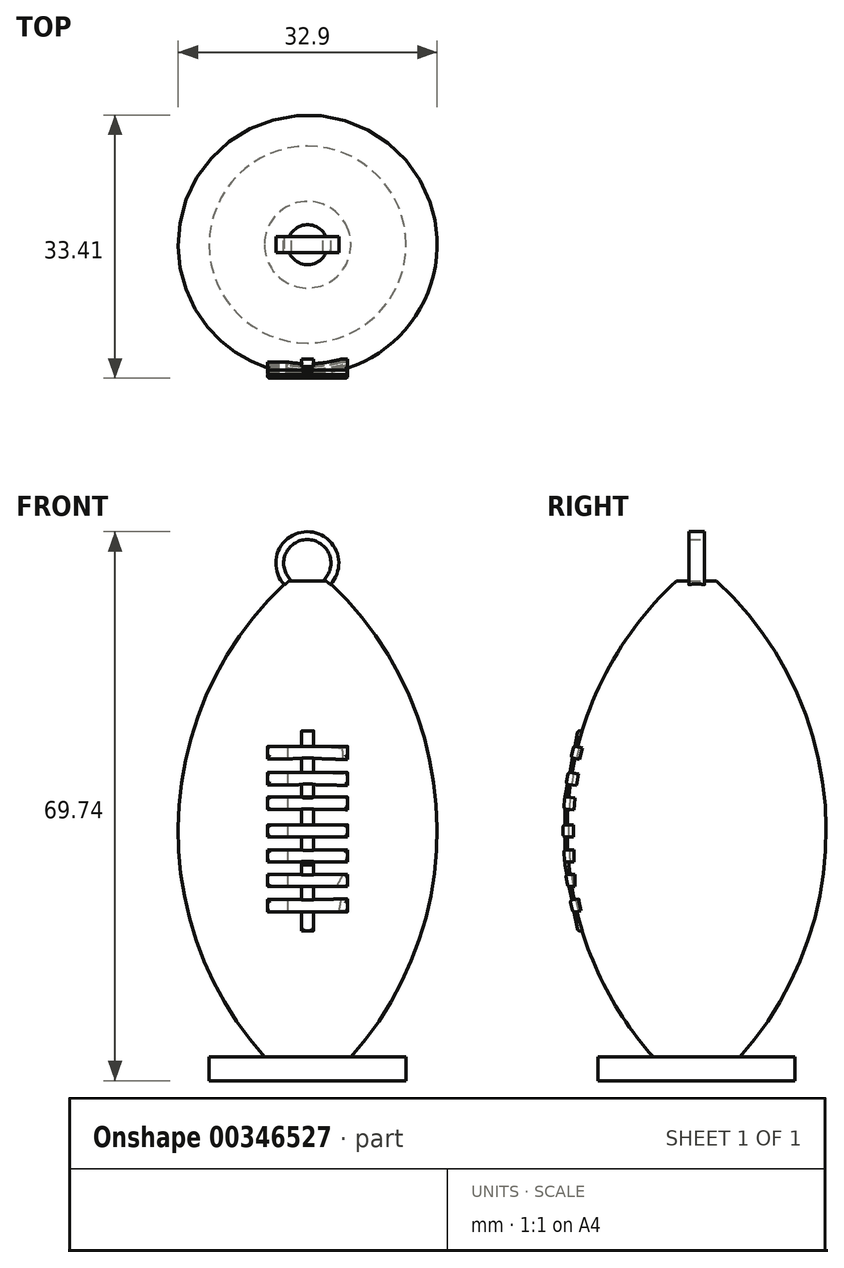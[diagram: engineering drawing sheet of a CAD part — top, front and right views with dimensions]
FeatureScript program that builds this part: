
annotation { "Feature Type Name" : "Feature", "Feature Type Description" : "" }
export const myFeature = defineFeature(function(context is Context, id is Id, definition is map)
    precondition{}
    {
        {
            var Q0;
            Q0=qCreatedBy(makeId("Front.planeOp"),FACE);
            var sketch = newSketch(context, id + "F0", { "sketchPlane" : qUnion([Q0])});
            skLineSegment(sketch, "E0", {"start": v(0, 0) * mm, "end": v(0, 63.5) * mm});
            skLineSegment(sketch, "E1", {"start": v(0, 0) * mm, "end": v(2.54, 0) * mm});
            skLineSegment(sketch, "E2", {"start": v(2.54, 0) * mm, "end": v(2.54, 63.5) * mm});
            skLineSegment(sketch, "E3", {"start": v(2.54, 63.5) * mm, "end": v(0, 63.5) * mm});
            skArc(sketch, "E4", {"start": v(0, 63.5) * mm, "mid": v(-13.91, 31.75) * mm, "end": v(0, 0) * mm});
            skSolve(sketch);
        }
        {
            var Q0;
            Q0=makeQuery(id+"F0.imprint","IMPRINT",FACE,{"disambiguationData":[TD([[makeQuery(id+"F0.imprint","IMPRINT",EDGE,{"derivedFrom":sQuery(id+"F0.wireOp",EDGE,"E0")}),1.0]])]});
            var Q1;
            Q1=sQuery(id+"F0.wireOp",EDGE,"E2");
            revolve(context, id + "F1", {"entities" : qUnion([Q0]), "axis" : qUnion([Q1]), "revolveType" : RevolveType.FULL});
        }
        {
            var Q0;
            Q0=qCreatedBy(makeId("Front.planeOp"),FACE);
            var sketch = newSketch(context, id + "F2", { "sketchPlane" : qUnion([Q0])});
            skLineSegment(sketch, "E5", {"start": v(0, 63.5) * mm, "end": v(2.54, 63.5) * mm});
            skLineSegment(sketch, "E6", {"start": v(0, 63.5) * mm, "end": v(2.03, 65.95) * mm});
            skLineSegment(sketch, "E7", {"start": v(2.03, 65.95) * mm, "end": v(2.54, 65.95) * mm});
            skLineSegment(sketch, "E8", {"start": v(2.54, 65.95) * mm, "end": v(2.54, 63.5) * mm});
            skLineSegment(sketch, "E9.left", {"start": v(0, 63.5) * mm, "end": v(0, 0) * mm});
            skLineSegment(sketch, "E9.right", {"start": v(2.54, 63.5) * mm, "end": v(2.54, 0) * mm});
            skLineSegment(sketch, "E10.bottom", {"start": v(0, 0) * mm, "end": v(2.54, 0) * mm});
            skLineSegment(sketch, "E10.top", {"start": v(0, -2.54) * mm, "end": v(2.54, -2.54) * mm});
            skLineSegment(sketch, "E10.left", {"start": v(0, 0) * mm, "end": v(0, -2.54) * mm});
            skLineSegment(sketch, "E10.right", {"start": v(2.54, 0) * mm, "end": v(2.54, -2.54) * mm});
            skSolve(sketch);
        }
        {
            var Q0;
            Q0=makeQuery(id+"F2.imprint","IMPRINT",FACE,{"disambiguationData":[TD([[makeQuery(id+"F2.imprint","IMPRINT",EDGE,{"derivedFrom":sQuery(id+"F2.wireOp",EDGE,"E5")}),-1.0]])]});
            var Q1;
            Q1=sQuery(id+"F2.wireOp",EDGE,"E9.right");
            revolve(context, id + "F3", {"operationType" : NewBodyOperationType.ADD, "entities" : qUnion([Q0]), "axis" : qUnion([Q1]), "revolveType" : RevolveType.FULL});
        }
        {
            var Q0;
            Q0=makeQuery(id+"F3.opRevolve","SWEPT_FACE",FACE,{"disambiguationData":[OSD([sQuery(id+"F2.wireOp",EDGE,"E10.bottom")])]});
            var sketch = newSketch(context, id + "F4", { "sketchPlane" : qUnion([Q0])});
            skLineSegment(sketch, "E11.bottom", {"start": v(4.34, -1.8) * mm, "end": v(0.74, -1.8) * mm});
            skLineSegment(sketch, "E11.top", {"start": v(4.34, 1.8) * mm, "end": v(0.74, 1.8) * mm});
            skLineSegment(sketch, "E11.left", {"start": v(4.34, -1.8) * mm, "end": v(4.34, 1.8) * mm});
            skLineSegment(sketch, "E11.right", {"start": v(0.74, -1.8) * mm, "end": v(0.74, 1.8) * mm});
            skPoint(sketch, "E11.middle", {"position": v(2.54, 0) * mm});
            skCircle(sketch, "E12", {"center": v(2.54, 0) * mm, "radius": 12.5 * mm});
            skSolve(sketch);
        }
        {
            var Q0;
            Q0=makeQuery(id+"F4.imprint","IMPRINT",FACE,{"disambiguationData":[TD([[makeQuery(id+"F4.imprint","IMPRINT",EDGE,{"derivedFrom":sQuery(id+"F4.wireOp",EDGE,"E11.bottom")}),-1.0]])]});
            var Q1;
            Q1=makeQuery(id+"F4.imprint","IMPRINT",FACE,{"disambiguationData":[TD([[makeQuery(id+"F4.imprint","IMPRINT",EDGE,{"derivedFrom":sQuery(id+"F4.wireOp",EDGE,"E12")}),1.0]])]});
            var Q2;
            {var subQ0=sQuery(id+"F4.wireOp",EDGE,"E11.bottom");Q2=makeQuery(id+"F4.imprint","IMPRINT",FACE,{"disambiguationData":[TD([[makeQuery(id+"F4.imprint","IMPRINT",EDGE,{"derivedFrom":subQ0}),1.0]])]});}
            var Q3;
            {var subQ0=sQuery(id+"F4.wireOp",EDGE,"E11.left");Q3=makeQuery(id+"F4.imprint","IMPRINT",FACE,{"disambiguationData":[TD([[makeQuery(id+"F4.imprint","IMPRINT",EDGE,{"derivedFrom":subQ0}),-1.0]])]});}
            var Q4;
            {var subQ0=sQuery(id+"F4.wireOp",EDGE,"E11.top");Q4=makeQuery(id+"F4.imprint","IMPRINT",FACE,{"disambiguationData":[TD([[makeQuery(id+"F4.imprint","IMPRINT",EDGE,{"derivedFrom":subQ0}),-1.0]])]});}
            var Q5;
            {var subQ0=sQuery(id+"F4.wireOp",EDGE,"E11.right");Q5=makeQuery(id+"F4.imprint","IMPRINT",FACE,{"disambiguationData":[TD([[makeQuery(id+"F4.imprint","IMPRINT",EDGE,{"derivedFrom":subQ0}),1.0]])]});}
            extrude(context, id + "F5", {"entities" : qUnion([Q0, Q1, Q2, Q3, Q4, Q5]), "operationType" : NewBodyOperationType.ADD, "oppositeDirection" : true, "depth" : 3 * mm, "offsetDistance" : 25 * mm});
        }
        {
            var Q0;
            Q0=qCreatedBy(makeId("Right.planeOp"),FACE);
            var sketch = newSketch(context, id + "F6", { "sketchPlane" : qUnion([Q0])});
            skLineSegment(sketch, "E13", {"start": v(0, 0) * mm, "end": v(0, 63.5) * mm});
            skLineSegment(sketch, "E14", {"start": v(0, 63.5) * mm, "end": v(-3.05, 63.5) * mm});
            skLineSegment(sketch, "E15", {"start": v(-3.05, 63.5) * mm, "end": v(-3.05, 0) * mm});
            skLineSegment(sketch, "E16", {"start": v(-3.05, 0) * mm, "end": v(0, 0) * mm});
            skArc(sketch, "E17", {"start": v(-3.05, 63.5) * mm, "mid": v(-16.96, 31.75) * mm, "end": v(-3.05, 0) * mm});
            skLineSegment(sketch, "E18.bottom", {"start": v(-16.96, 32.51) * mm, "end": v(-15.63, 32.51) * mm});
            skLineSegment(sketch, "E18.top", {"start": v(-16.96, 30.99) * mm, "end": v(-15.63, 30.99) * mm});
            skLineSegment(sketch, "E18.left", {"start": v(-16.96, 32.51) * mm, "end": v(-16.96, 30.99) * mm});
            skLineSegment(sketch, "E18.right", {"start": v(-15.63, 32.51) * mm, "end": v(-15.63, 30.99) * mm});
            skLineSegment(sketch, "E19", {"start": v(-15.2, 34.39) * mm, "end": v(-15.08, 35.9) * mm});
            skLineSegment(sketch, "E20", {"start": v(-15.08, 35.9) * mm, "end": v(-16.75, 36.04) * mm});
            skLineSegment(sketch, "E21", {"start": v(-16.75, 36.04) * mm, "end": v(-16.87, 34.52) * mm});
            skLineSegment(sketch, "E22", {"start": v(-16.87, 34.52) * mm, "end": v(-15.2, 34.39) * mm});
            skLineSegment(sketch, "E23", {"start": v(-16.55, 37.68) * mm, "end": v(-16.32, 39.19) * mm});
            skLineSegment(sketch, "E24", {"start": v(-16.32, 39.19) * mm, "end": v(-14.98, 38.98) * mm});
            skLineSegment(sketch, "E25", {"start": v(-14.98, 38.98) * mm, "end": v(-15.21, 37.47) * mm});
            skLineSegment(sketch, "E26", {"start": v(-15.21, 37.47) * mm, "end": v(-16.55, 37.68) * mm});
            skLineSegment(sketch, "E27", {"start": v(-16.9, 29.29) * mm, "end": v(-15.57, 29.29) * mm});
            skLineSegment(sketch, "E28", {"start": v(-15.57, 29.29) * mm, "end": v(-15.57, 27.77) * mm});
            skLineSegment(sketch, "E29", {"start": v(-15.57, 27.77) * mm, "end": v(-16.78, 27.77) * mm});
            skLineSegment(sketch, "E30", {"start": v(-16.78, 27.77) * mm, "end": v(-16.9, 29.29) * mm});
            skLineSegment(sketch, "E31", {"start": v(-16.6, 26.22) * mm, "end": v(-15.46, 26.22) * mm});
            skLineSegment(sketch, "E32", {"start": v(-15.46, 26.22) * mm, "end": v(-15.46, 24.7) * mm});
            skLineSegment(sketch, "E33", {"start": v(-15.46, 24.7) * mm, "end": v(-16.38, 24.7) * mm});
            skLineSegment(sketch, "E34", {"start": v(-16.38, 24.7) * mm, "end": v(-16.6, 26.22) * mm});
            skLineSegment(sketch, "E35", {"start": v(-15.95, 41.04) * mm, "end": v(-15.6, 42.52) * mm});
            skLineSegment(sketch, "E36", {"start": v(-15.6, 42.52) * mm, "end": v(-14.5, 42.26) * mm});
            skLineSegment(sketch, "E37", {"start": v(-14.5, 42.26) * mm, "end": v(-14.86, 40.78) * mm});
            skLineSegment(sketch, "E38", {"start": v(-14.86, 40.78) * mm, "end": v(-15.95, 41.04) * mm});
            skLineSegment(sketch, "E39", {"start": v(-16.05, 22.93) * mm, "end": v(-15.7, 21.42) * mm});
            skLineSegment(sketch, "E40", {"start": v(-15.7, 21.42) * mm, "end": v(-14.71, 21.6) * mm});
            skLineSegment(sketch, "E41", {"start": v(-14.71, 21.6) * mm, "end": v(-14.98, 23.1) * mm});
            skLineSegment(sketch, "E42", {"start": v(-14.98, 23.1) * mm, "end": v(-16.05, 22.93) * mm});
            skSolve(sketch);
        }
        {
            var Q0;
            Q0=makeQuery(id+"F6.imprint","IMPRINT",FACE,{"disambiguationData":[TD([[makeQuery(id+"F6.imprint","IMPRINT",EDGE,{"derivedFrom":sQuery(id+"F6.wireOp",EDGE,"E35")}),-1.0]])]});
            var Q1;
            {var subQ0=sQuery(id+"F6.wireOp",EDGE,"E25");Q1=makeQuery(id+"F6.imprint","IMPRINT",FACE,{"disambiguationData":[TD([[makeQuery(id+"F6.imprint","IMPRINT",EDGE,{"derivedFrom":subQ0}),-1.0]])]});}
            var Q2;
            Q2=makeQuery(id+"F6.imprint","IMPRINT",FACE,{"disambiguationData":[TD([[makeQuery(id+"F6.imprint","IMPRINT",EDGE,{"derivedFrom":sQuery(id+"F6.wireOp",EDGE,"E19")}),1.0]])]});
            var Q3;
            Q3=makeQuery(id+"F6.imprint","IMPRINT",FACE,{"disambiguationData":[TD([[makeQuery(id+"F6.imprint","IMPRINT",EDGE,{"derivedFrom":sQuery(id+"F6.wireOp",EDGE,"E18.bottom")}),-1.0]])]});
            var Q4;
            Q4=makeQuery(id+"F6.imprint","IMPRINT",FACE,{"disambiguationData":[TD([[makeQuery(id+"F6.imprint","IMPRINT",EDGE,{"derivedFrom":sQuery(id+"F6.wireOp",EDGE,"E27")}),-1.0]])]});
            var Q5;
            Q5=makeQuery(id+"F6.imprint","IMPRINT",FACE,{"disambiguationData":[TD([[makeQuery(id+"F6.imprint","IMPRINT",EDGE,{"derivedFrom":sQuery(id+"F6.wireOp",EDGE,"E31")}),-1.0]])]});
            var Q6;
            Q6=makeQuery(id+"F6.imprint","IMPRINT",FACE,{"disambiguationData":[TD([[makeQuery(id+"F6.imprint","IMPRINT",EDGE,{"derivedFrom":sQuery(id+"F6.wireOp",EDGE,"E39")}),1.0]])]});
            extrude(context, id + "F7", {"entities" : qUnion([Q0, Q1, Q2, Q3, Q4, Q5, Q6]), "operationType" : NewBodyOperationType.ADD, "depth" : 7.62 * mm});
        }
        {
            var Q0;
            Q0=makeQuery(id+"F7.opExtrude","CAP_FACE",FACE,{"disambiguationData":[OSD([sQuery(id+"F6.wireOp",EDGE,"E35"),sQuery(id+"F6.wireOp",EDGE,"E36"),sQuery(id+"F6.wireOp",EDGE,"E37"),sQuery(id+"F6.wireOp",EDGE,"E38")])],"isStart":true});
            var Q1;
            Q1=makeQuery(id+"F7.opExtrude","CAP_FACE",FACE,{"disambiguationData":[OSD([sQuery(id+"F6.wireOp",EDGE,"E17"),sQuery(id+"F6.wireOp",EDGE,"E23"),sQuery(id+"F6.wireOp",EDGE,"E24"),sQuery(id+"F6.wireOp",EDGE,"E25"),sQuery(id+"F6.wireOp",EDGE,"E26")])],"isStart":true});
            var Q2;
            Q2=makeQuery(id+"F7.opExtrude","CAP_FACE",FACE,{"disambiguationData":[OSD([sQuery(id+"F6.wireOp",EDGE,"E19"),sQuery(id+"F6.wireOp",EDGE,"E20"),sQuery(id+"F6.wireOp",EDGE,"E21"),sQuery(id+"F6.wireOp",EDGE,"E22")])],"isStart":true});
            var Q3;
            Q3=makeQuery(id+"F7.opExtrude","CAP_FACE",FACE,{"disambiguationData":[OSD([sQuery(id+"F6.wireOp",EDGE,"E18.bottom"),sQuery(id+"F6.wireOp",EDGE,"E18.top"),sQuery(id+"F6.wireOp",EDGE,"E18.left"),sQuery(id+"F6.wireOp",EDGE,"E18.right")])],"isStart":true});
            var Q4;
            Q4=makeQuery(id+"F7.opExtrude","CAP_FACE",FACE,{"disambiguationData":[OSD([sQuery(id+"F6.wireOp",EDGE,"E27"),sQuery(id+"F6.wireOp",EDGE,"E28"),sQuery(id+"F6.wireOp",EDGE,"E29"),sQuery(id+"F6.wireOp",EDGE,"E30")])],"isStart":true});
            var Q5;
            Q5=makeQuery(id+"F7.opExtrude","CAP_FACE",FACE,{"disambiguationData":[OSD([sQuery(id+"F6.wireOp",EDGE,"E31"),sQuery(id+"F6.wireOp",EDGE,"E32"),sQuery(id+"F6.wireOp",EDGE,"E33"),sQuery(id+"F6.wireOp",EDGE,"E34")])],"isStart":true});
            var Q6;
            Q6=makeQuery(id+"F7.opExtrude","CAP_FACE",FACE,{"disambiguationData":[OSD([sQuery(id+"F6.wireOp",EDGE,"E39"),sQuery(id+"F6.wireOp",EDGE,"E40"),sQuery(id+"F6.wireOp",EDGE,"E41"),sQuery(id+"F6.wireOp",EDGE,"E42")])],"isStart":true});
            extrude(context, id + "F8", {"entities" : qUnion([Q0, Q1, Q2, Q3, Q4, Q5, Q6]), "operationType" : NewBodyOperationType.ADD, "depth" : 2.54 * mm});
        }
        {
            var Q0;
            {var subQ0=sQuery(id+"F6.wireOp",EDGE,"E18.left");Q0=makeQuery(id+"F8.boolean.opBoolean","MERGE",FACE,{"derivedFrom":[makeQuery(id+"F7.opExtrude","SWEPT_FACE",FACE,{"disambiguationData":[OSD([subQ0])]}),makeQuery(id+"F8.opExtrude","SWEPT_FACE",FACE,{"disambiguationData":[OSD([subQ0])]})]});}
            var sketch = newSketch(context, id + "F9", { "sketchPlane" : qUnion([Q0])});
            skLineSegment(sketch, "E43.bottom", {"start": v(3.3, 19.05) * mm, "end": v(1.78, 19.05) * mm});
            skLineSegment(sketch, "E43.top", {"start": v(3.3, 44.45) * mm, "end": v(1.78, 44.45) * mm});
            skLineSegment(sketch, "E43.left", {"start": v(3.3, 19.05) * mm, "end": v(3.3, 44.45) * mm});
            skLineSegment(sketch, "E43.right", {"start": v(1.78, 19.05) * mm, "end": v(1.78, 44.45) * mm});
            skPoint(sketch, "E43.middle", {"position": v(2.54, 31.75) * mm});
            skPoint(sketch, "E43.middle.positionSnap0", {"position": v(7.62, 31.75) * mm});
            skPoint(sketch, "E43.middle.positionSnap1", {"position": v(2.54, 32.51) * mm});
            skPoint(sketch, "E43.centerSnap0", {"position": v(7.62, 31.75) * mm});
            skPoint(sketch, "E43.centerSnap1", {"position": v(2.54, 32.51) * mm});
            skSolve(sketch);
        }
        {
            var Q0;
            {var subQ0=sQuery(id+"F9.wireOp",EDGE,"E43.top");Q0=makeQuery(id+"F9.imprint","IMPRINT",FACE,{"disambiguationData":[TD([[makeQuery(id+"F9.imprint","IMPRINT",EDGE,{"derivedFrom":subQ0}),1.0]])]});}
            var Q1;
            {var subQ0=sQuery(id+"F9.wireOp",EDGE,"E43.bottom");Q1=makeQuery(id+"F9.imprint","IMPRINT",FACE,{"disambiguationData":[TD([[makeQuery(id+"F9.imprint","IMPRINT",EDGE,{"derivedFrom":subQ0}),-1.0]])]});}
            var Q2;
            {var subQ0=sQuery(id+"F9.wireOp",EDGE,"E43.left");var subQ1=sQuery(id+"F6.wireOp",EDGE,"E18.left");var subQ2=sQuery(id+"F6.wireOp",EDGE,"E18.top");var subQ3=sQuery(id+"F6.wireOp",EDGE,"E17");var subQ4=makeQuery(id+"F8.boolean.opBoolean","MERGE",EDGE,{"derivedFrom":[makeQuery(id+"F7.opExtrude","SWEPT_EDGE",EDGE,{"disambiguationData":[OSD([subQ3,subQ2,subQ1])]}),makeQuery(id+"F8.opExtrude","SWEPT_EDGE",EDGE,{"disambiguationData":[OSD([subQ3,subQ2,subQ1])]})]});var subQ5=makeQuery(id+"F9.imprint","INTERSECT",VERTEX,{"derivedFrom":[subQ4,subQ0]});Q2=makeQuery(id+"F9.imprint","IMPRINT",FACE,{"disambiguationData":[TD([[makeQuery(id+"F9.imprint","IMPRINT",EDGE,{"disambiguationData":[TD([[subQ5,-1.0]])],"derivedFrom":subQ0}),1.0]])]});}
            extrude(context, id + "F10", {"entities" : qUnion([Q0, Q1, Q2]), "operationType" : NewBodyOperationType.ADD, "oppositeDirection" : true, "depth" : 2.54 * mm});
        }
        {
            var Q0;
            {var subQ0=sQuery(id+"F6.wireOp",EDGE,"E24");var subQ1=sQuery(id+"F6.wireOp",EDGE,"E17");Q0=makeQuery(id+"F10.boolean.opBoolean","SPLIT",EDGE,{"disambiguationData":[TD([makeQuery(id+"F10.opExtrude","SWEPT_FACE",FACE,{"disambiguationData":[OSD([sQuery(id+"F9.wireOp",EDGE,"E43.left")])]})])],"derivedFrom":makeQuery(id+"F8.boolean.opBoolean","MERGE",EDGE,{"derivedFrom":[makeQuery(id+"F7.opExtrude","SWEPT_EDGE",EDGE,{"disambiguationData":[OSD([subQ1,subQ0])]}),makeQuery(id+"F8.opExtrude","SWEPT_EDGE",EDGE,{"disambiguationData":[OSD([subQ1,subQ0])]})]})});}
            var Q1;
            Q1=makeQuery(id+"F7.opExtrude","CAP_EDGE",EDGE,{"disambiguationData":[OSD([sQuery(id+"F6.wireOp",EDGE,"E23")])],"isStart":false});
            var Q2;
            {var subQ0=sQuery(id+"F6.wireOp",EDGE,"E26");var subQ1=sQuery(id+"F6.wireOp",EDGE,"E23");var subQ2=sQuery(id+"F6.wireOp",EDGE,"E17");Q2=makeQuery(id+"F10.boolean.opBoolean","SPLIT",EDGE,{"disambiguationData":[TD([makeQuery(id+"F10.opExtrude","SWEPT_FACE",FACE,{"disambiguationData":[OSD([sQuery(id+"F9.wireOp",EDGE,"E43.left")])]})])],"derivedFrom":makeQuery(id+"F8.boolean.opBoolean","MERGE",EDGE,{"derivedFrom":[makeQuery(id+"F7.opExtrude","SWEPT_EDGE",EDGE,{"disambiguationData":[OSD([subQ2,subQ1,subQ0])]}),makeQuery(id+"F8.opExtrude","SWEPT_EDGE",EDGE,{"disambiguationData":[OSD([subQ2,subQ1,subQ0])]})]})});}
            var Q3;
            {var subQ0=sQuery(id+"F6.wireOp",EDGE,"E24");var subQ1=sQuery(id+"F6.wireOp",EDGE,"E17");Q3=makeQuery(id+"F10.boolean.opBoolean","SPLIT",EDGE,{"disambiguationData":[TD([makeQuery(id+"F10.opExtrude","SWEPT_FACE",FACE,{"disambiguationData":[OSD([sQuery(id+"F9.wireOp",EDGE,"E43.right")])]})])],"derivedFrom":makeQuery(id+"F8.boolean.opBoolean","MERGE",EDGE,{"derivedFrom":[makeQuery(id+"F7.opExtrude","SWEPT_EDGE",EDGE,{"disambiguationData":[OSD([subQ1,subQ0])]}),makeQuery(id+"F8.opExtrude","SWEPT_EDGE",EDGE,{"disambiguationData":[OSD([subQ1,subQ0])]})]})});}
            var Q4;
            {var subQ0=sQuery(id+"F6.wireOp",EDGE,"E26");var subQ1=sQuery(id+"F6.wireOp",EDGE,"E23");var subQ2=sQuery(id+"F6.wireOp",EDGE,"E17");Q4=makeQuery(id+"F10.boolean.opBoolean","SPLIT",EDGE,{"disambiguationData":[TD([makeQuery(id+"F10.opExtrude","SWEPT_FACE",FACE,{"disambiguationData":[OSD([sQuery(id+"F9.wireOp",EDGE,"E43.right")])]})])],"derivedFrom":makeQuery(id+"F8.boolean.opBoolean","MERGE",EDGE,{"derivedFrom":[makeQuery(id+"F7.opExtrude","SWEPT_EDGE",EDGE,{"disambiguationData":[OSD([subQ2,subQ1,subQ0])]}),makeQuery(id+"F8.opExtrude","SWEPT_EDGE",EDGE,{"disambiguationData":[OSD([subQ2,subQ1,subQ0])]})]})});}
            var Q5;
            Q5=makeQuery(id+"F8.opExtrude","CAP_EDGE",EDGE,{"disambiguationData":[OSD([sQuery(id+"F6.wireOp",EDGE,"E23")])],"isStart":false});
            var Q6;
            Q6=makeQuery(id+"F8.opExtrude","CAP_EDGE",EDGE,{"disambiguationData":[OSD([sQuery(id+"F6.wireOp",EDGE,"E17")])],"isStart":false});
            var Q7;
            Q7=makeQuery(id+"F7.opExtrude","CAP_EDGE",EDGE,{"disambiguationData":[OSD([sQuery(id+"F6.wireOp",EDGE,"E17")])],"isStart":false});
            var Q8;
            {var subQ0=sQuery(id+"F6.wireOp",EDGE,"E36");var subQ1=sQuery(id+"F6.wireOp",EDGE,"E35");var subQ2=sQuery(id+"F6.wireOp",EDGE,"E17");Q8=makeQuery(id+"F10.boolean.opBoolean","SPLIT",EDGE,{"disambiguationData":[TD([makeQuery(id+"F10.opExtrude","SWEPT_FACE",FACE,{"disambiguationData":[OSD([sQuery(id+"F9.wireOp",EDGE,"E43.right")])]})])],"derivedFrom":makeQuery(id+"F8.boolean.opBoolean","MERGE",EDGE,{"derivedFrom":[makeQuery(id+"F7.opExtrude","SWEPT_EDGE",EDGE,{"disambiguationData":[OSD([subQ2,subQ1,subQ0])]}),makeQuery(id+"F8.opExtrude","SWEPT_EDGE",EDGE,{"disambiguationData":[OSD([subQ2,subQ1,subQ0])]})]})});}
            var Q9;
            {var subQ0=sQuery(id+"F6.wireOp",EDGE,"E35");var subQ1=sQuery(id+"F6.wireOp",EDGE,"E38");var subQ2=sQuery(id+"F6.wireOp",EDGE,"E17");Q9=makeQuery(id+"F10.boolean.opBoolean","SPLIT",EDGE,{"disambiguationData":[TD([makeQuery(id+"F10.opExtrude","SWEPT_FACE",FACE,{"disambiguationData":[OSD([sQuery(id+"F9.wireOp",EDGE,"E43.right")])]})])],"derivedFrom":makeQuery(id+"F8.boolean.opBoolean","MERGE",EDGE,{"derivedFrom":[makeQuery(id+"F7.opExtrude","SWEPT_EDGE",EDGE,{"disambiguationData":[OSD([subQ2,subQ0,subQ1])]}),makeQuery(id+"F8.opExtrude","SWEPT_EDGE",EDGE,{"disambiguationData":[OSD([subQ2,subQ0,subQ1])]})]})});}
            var Q10;
            Q10=makeQuery(id+"F8.opExtrude","CAP_EDGE",EDGE,{"disambiguationData":[OSD([sQuery(id+"F6.wireOp",EDGE,"E35")])],"isStart":false});
            var Q11;
            {var subQ0=sQuery(id+"F6.wireOp",EDGE,"E36");var subQ1=sQuery(id+"F6.wireOp",EDGE,"E35");var subQ2=sQuery(id+"F6.wireOp",EDGE,"E17");Q11=makeQuery(id+"F10.boolean.opBoolean","SPLIT",EDGE,{"disambiguationData":[TD([makeQuery(id+"F10.opExtrude","SWEPT_FACE",FACE,{"disambiguationData":[OSD([sQuery(id+"F9.wireOp",EDGE,"E43.left")])]})])],"derivedFrom":makeQuery(id+"F8.boolean.opBoolean","MERGE",EDGE,{"derivedFrom":[makeQuery(id+"F7.opExtrude","SWEPT_EDGE",EDGE,{"disambiguationData":[OSD([subQ2,subQ1,subQ0])]}),makeQuery(id+"F8.opExtrude","SWEPT_EDGE",EDGE,{"disambiguationData":[OSD([subQ2,subQ1,subQ0])]})]})});}
            var Q12;
            {var subQ0=sQuery(id+"F6.wireOp",EDGE,"E35");var subQ1=sQuery(id+"F6.wireOp",EDGE,"E38");var subQ2=sQuery(id+"F6.wireOp",EDGE,"E17");Q12=makeQuery(id+"F10.boolean.opBoolean","SPLIT",EDGE,{"disambiguationData":[TD([makeQuery(id+"F10.opExtrude","SWEPT_FACE",FACE,{"disambiguationData":[OSD([sQuery(id+"F9.wireOp",EDGE,"E43.left")])]})])],"derivedFrom":makeQuery(id+"F8.boolean.opBoolean","MERGE",EDGE,{"derivedFrom":[makeQuery(id+"F7.opExtrude","SWEPT_EDGE",EDGE,{"disambiguationData":[OSD([subQ2,subQ0,subQ1])]}),makeQuery(id+"F8.opExtrude","SWEPT_EDGE",EDGE,{"disambiguationData":[OSD([subQ2,subQ0,subQ1])]})]})});}
            var Q13;
            Q13=makeQuery(id+"F7.opExtrude","CAP_EDGE",EDGE,{"disambiguationData":[OSD([sQuery(id+"F6.wireOp",EDGE,"E35")])],"isStart":false});
            var Q14;
            {var subQ0=sQuery(id+"F6.wireOp",EDGE,"E21");var subQ1=sQuery(id+"F6.wireOp",EDGE,"E20");var subQ2=sQuery(id+"F6.wireOp",EDGE,"E17");Q14=makeQuery(id+"F10.boolean.opBoolean","SPLIT",EDGE,{"disambiguationData":[TD([makeQuery(id+"F10.opExtrude","SWEPT_FACE",FACE,{"disambiguationData":[OSD([sQuery(id+"F9.wireOp",EDGE,"E43.right")])]})])],"derivedFrom":makeQuery(id+"F8.boolean.opBoolean","MERGE",EDGE,{"derivedFrom":[makeQuery(id+"F7.opExtrude","SWEPT_EDGE",EDGE,{"disambiguationData":[OSD([subQ2,subQ1,subQ0])]}),makeQuery(id+"F8.opExtrude","SWEPT_EDGE",EDGE,{"disambiguationData":[OSD([subQ2,subQ1,subQ0])]})]})});}
            var Q15;
            Q15=makeQuery(id+"F8.opExtrude","CAP_EDGE",EDGE,{"disambiguationData":[OSD([sQuery(id+"F6.wireOp",EDGE,"E21")])],"isStart":false});
            var Q16;
            {var subQ0=sQuery(id+"F6.wireOp",EDGE,"E21");var subQ1=sQuery(id+"F6.wireOp",EDGE,"E22");var subQ2=sQuery(id+"F6.wireOp",EDGE,"E17");Q16=makeQuery(id+"F10.boolean.opBoolean","SPLIT",EDGE,{"disambiguationData":[TD([makeQuery(id+"F10.opExtrude","SWEPT_FACE",FACE,{"disambiguationData":[OSD([sQuery(id+"F9.wireOp",EDGE,"E43.right")])]})])],"derivedFrom":makeQuery(id+"F8.boolean.opBoolean","MERGE",EDGE,{"derivedFrom":[makeQuery(id+"F7.opExtrude","SWEPT_EDGE",EDGE,{"disambiguationData":[OSD([subQ2,subQ0,subQ1])]}),makeQuery(id+"F8.opExtrude","SWEPT_EDGE",EDGE,{"disambiguationData":[OSD([subQ2,subQ0,subQ1])]})]})});}
            var Q17;
            {var subQ0=sQuery(id+"F6.wireOp",EDGE,"E21");var subQ1=sQuery(id+"F6.wireOp",EDGE,"E20");var subQ2=sQuery(id+"F6.wireOp",EDGE,"E17");Q17=makeQuery(id+"F10.boolean.opBoolean","SPLIT",EDGE,{"disambiguationData":[TD([makeQuery(id+"F10.opExtrude","SWEPT_FACE",FACE,{"disambiguationData":[OSD([sQuery(id+"F9.wireOp",EDGE,"E43.left")])]})])],"derivedFrom":makeQuery(id+"F8.boolean.opBoolean","MERGE",EDGE,{"derivedFrom":[makeQuery(id+"F7.opExtrude","SWEPT_EDGE",EDGE,{"disambiguationData":[OSD([subQ2,subQ1,subQ0])]}),makeQuery(id+"F8.opExtrude","SWEPT_EDGE",EDGE,{"disambiguationData":[OSD([subQ2,subQ1,subQ0])]})]})});}
            var Q18;
            {var subQ0=sQuery(id+"F6.wireOp",EDGE,"E21");var subQ1=sQuery(id+"F6.wireOp",EDGE,"E22");var subQ2=sQuery(id+"F6.wireOp",EDGE,"E17");Q18=makeQuery(id+"F10.boolean.opBoolean","SPLIT",EDGE,{"disambiguationData":[TD([makeQuery(id+"F10.opExtrude","SWEPT_FACE",FACE,{"disambiguationData":[OSD([sQuery(id+"F9.wireOp",EDGE,"E43.left")])]})])],"derivedFrom":makeQuery(id+"F8.boolean.opBoolean","MERGE",EDGE,{"derivedFrom":[makeQuery(id+"F7.opExtrude","SWEPT_EDGE",EDGE,{"disambiguationData":[OSD([subQ2,subQ0,subQ1])]}),makeQuery(id+"F8.opExtrude","SWEPT_EDGE",EDGE,{"disambiguationData":[OSD([subQ2,subQ0,subQ1])]})]})});}
            var Q19;
            Q19=makeQuery(id+"F7.opExtrude","CAP_EDGE",EDGE,{"disambiguationData":[OSD([sQuery(id+"F6.wireOp",EDGE,"E21")])],"isStart":false});
            var Q20;
            {var subQ0=sQuery(id+"F6.wireOp",EDGE,"E18.bottom");var subQ1=sQuery(id+"F6.wireOp",EDGE,"E18.left");var subQ2=sQuery(id+"F9.wireOp",EDGE,"E43.right");var subQ3=sQuery(id+"F6.wireOp",EDGE,"E17");Q20=makeQuery(id+"F10.boolean.opBoolean","SPLIT",EDGE,{"disambiguationData":[TD([makeQuery(id+"F10.opExtrude","SWEPT_FACE",FACE,{"disambiguationData":[OSD([subQ2])]})])],"derivedFrom":makeQuery(id+"F8.boolean.opBoolean","MERGE",EDGE,{"derivedFrom":[makeQuery(id+"F7.opExtrude","SWEPT_EDGE",EDGE,{"disambiguationData":[OSD([subQ3,subQ0,subQ1])]}),makeQuery(id+"F8.opExtrude","SWEPT_EDGE",EDGE,{"disambiguationData":[OSD([subQ3,subQ0,subQ1])]})]})});}
            var Q21;
            Q21=makeQuery(id+"F8.opExtrude","CAP_EDGE",EDGE,{"disambiguationData":[OSD([sQuery(id+"F6.wireOp",EDGE,"E18.left")])],"isStart":false});
            var Q22;
            {var subQ0=sQuery(id+"F6.wireOp",EDGE,"E18.left");var subQ1=sQuery(id+"F6.wireOp",EDGE,"E18.top");var subQ2=sQuery(id+"F9.wireOp",EDGE,"E43.right");var subQ3=sQuery(id+"F6.wireOp",EDGE,"E17");Q22=makeQuery(id+"F10.boolean.opBoolean","SPLIT",EDGE,{"disambiguationData":[TD([makeQuery(id+"F10.opExtrude","SWEPT_FACE",FACE,{"disambiguationData":[OSD([subQ2])]})])],"derivedFrom":makeQuery(id+"F8.boolean.opBoolean","MERGE",EDGE,{"derivedFrom":[makeQuery(id+"F7.opExtrude","SWEPT_EDGE",EDGE,{"disambiguationData":[OSD([subQ3,subQ1,subQ0])]}),makeQuery(id+"F8.opExtrude","SWEPT_EDGE",EDGE,{"disambiguationData":[OSD([subQ3,subQ1,subQ0])]})]})});}
            var Q23;
            {var subQ0=sQuery(id+"F6.wireOp",EDGE,"E18.left");var subQ1=sQuery(id+"F6.wireOp",EDGE,"E18.top");var subQ2=sQuery(id+"F9.wireOp",EDGE,"E43.left");var subQ3=sQuery(id+"F6.wireOp",EDGE,"E17");Q23=makeQuery(id+"F10.boolean.opBoolean","SPLIT",EDGE,{"disambiguationData":[TD([makeQuery(id+"F10.opExtrude","SWEPT_FACE",FACE,{"disambiguationData":[OSD([subQ2])]})])],"derivedFrom":makeQuery(id+"F8.boolean.opBoolean","MERGE",EDGE,{"derivedFrom":[makeQuery(id+"F7.opExtrude","SWEPT_EDGE",EDGE,{"disambiguationData":[OSD([subQ3,subQ1,subQ0])]}),makeQuery(id+"F8.opExtrude","SWEPT_EDGE",EDGE,{"disambiguationData":[OSD([subQ3,subQ1,subQ0])]})]})});}
            var Q24;
            {var subQ0=sQuery(id+"F6.wireOp",EDGE,"E18.left");var subQ1=sQuery(id+"F6.wireOp",EDGE,"E18.bottom");var subQ2=sQuery(id+"F9.wireOp",EDGE,"E43.left");var subQ3=sQuery(id+"F6.wireOp",EDGE,"E17");Q24=makeQuery(id+"F10.boolean.opBoolean","SPLIT",EDGE,{"disambiguationData":[TD([makeQuery(id+"F10.opExtrude","SWEPT_FACE",FACE,{"disambiguationData":[OSD([subQ2])]})])],"derivedFrom":makeQuery(id+"F8.boolean.opBoolean","MERGE",EDGE,{"derivedFrom":[makeQuery(id+"F7.opExtrude","SWEPT_EDGE",EDGE,{"disambiguationData":[OSD([subQ3,subQ1,subQ0])]}),makeQuery(id+"F8.opExtrude","SWEPT_EDGE",EDGE,{"disambiguationData":[OSD([subQ3,subQ1,subQ0])]})]})});}
            var Q25;
            Q25=makeQuery(id+"F7.opExtrude","CAP_EDGE",EDGE,{"disambiguationData":[OSD([sQuery(id+"F6.wireOp",EDGE,"E18.left")])],"isStart":false});
            var Q26;
            {var subQ0=sQuery(id+"F6.wireOp",EDGE,"E30");var subQ1=sQuery(id+"F6.wireOp",EDGE,"E27");var subQ2=sQuery(id+"F6.wireOp",EDGE,"E17");Q26=makeQuery(id+"F10.boolean.opBoolean","SPLIT",EDGE,{"disambiguationData":[TD([makeQuery(id+"F10.opExtrude","SWEPT_FACE",FACE,{"disambiguationData":[OSD([sQuery(id+"F9.wireOp",EDGE,"E43.left")])]})])],"derivedFrom":makeQuery(id+"F8.boolean.opBoolean","MERGE",EDGE,{"derivedFrom":[makeQuery(id+"F7.opExtrude","SWEPT_EDGE",EDGE,{"disambiguationData":[OSD([subQ2,subQ1,subQ0])]}),makeQuery(id+"F8.opExtrude","SWEPT_EDGE",EDGE,{"disambiguationData":[OSD([subQ2,subQ1,subQ0])]})]})});}
            var Q27;
            {var subQ0=sQuery(id+"F6.wireOp",EDGE,"E30");var subQ1=sQuery(id+"F6.wireOp",EDGE,"E29");var subQ2=sQuery(id+"F6.wireOp",EDGE,"E17");Q27=makeQuery(id+"F10.boolean.opBoolean","SPLIT",EDGE,{"disambiguationData":[TD([makeQuery(id+"F10.opExtrude","SWEPT_FACE",FACE,{"disambiguationData":[OSD([sQuery(id+"F9.wireOp",EDGE,"E43.left")])]})])],"derivedFrom":makeQuery(id+"F8.boolean.opBoolean","MERGE",EDGE,{"derivedFrom":[makeQuery(id+"F7.opExtrude","SWEPT_EDGE",EDGE,{"disambiguationData":[OSD([subQ2,subQ1,subQ0])]}),makeQuery(id+"F8.opExtrude","SWEPT_EDGE",EDGE,{"disambiguationData":[OSD([subQ2,subQ1,subQ0])]})]})});}
            var Q28;
            Q28=makeQuery(id+"F7.opExtrude","CAP_EDGE",EDGE,{"disambiguationData":[OSD([sQuery(id+"F6.wireOp",EDGE,"E30")])],"isStart":false});
            var Q29;
            {var subQ0=sQuery(id+"F6.wireOp",EDGE,"E27");var subQ1=sQuery(id+"F6.wireOp",EDGE,"E30");var subQ2=sQuery(id+"F6.wireOp",EDGE,"E17");Q29=makeQuery(id+"F10.boolean.opBoolean","SPLIT",EDGE,{"disambiguationData":[TD([makeQuery(id+"F10.opExtrude","SWEPT_FACE",FACE,{"disambiguationData":[OSD([sQuery(id+"F9.wireOp",EDGE,"E43.right")])]})])],"derivedFrom":makeQuery(id+"F8.boolean.opBoolean","MERGE",EDGE,{"derivedFrom":[makeQuery(id+"F7.opExtrude","SWEPT_EDGE",EDGE,{"disambiguationData":[OSD([subQ2,subQ0,subQ1])]}),makeQuery(id+"F8.opExtrude","SWEPT_EDGE",EDGE,{"disambiguationData":[OSD([subQ2,subQ0,subQ1])]})]})});}
            var Q30;
            {var subQ0=sQuery(id+"F6.wireOp",EDGE,"E29");var subQ1=sQuery(id+"F6.wireOp",EDGE,"E30");var subQ2=sQuery(id+"F6.wireOp",EDGE,"E17");Q30=makeQuery(id+"F10.boolean.opBoolean","SPLIT",EDGE,{"disambiguationData":[TD([makeQuery(id+"F10.opExtrude","SWEPT_FACE",FACE,{"disambiguationData":[OSD([sQuery(id+"F9.wireOp",EDGE,"E43.right")])]})])],"derivedFrom":makeQuery(id+"F8.boolean.opBoolean","MERGE",EDGE,{"derivedFrom":[makeQuery(id+"F7.opExtrude","SWEPT_EDGE",EDGE,{"disambiguationData":[OSD([subQ2,subQ0,subQ1])]}),makeQuery(id+"F8.opExtrude","SWEPT_EDGE",EDGE,{"disambiguationData":[OSD([subQ2,subQ0,subQ1])]})]})});}
            var Q31;
            Q31=makeQuery(id+"F8.opExtrude","CAP_EDGE",EDGE,{"disambiguationData":[OSD([sQuery(id+"F6.wireOp",EDGE,"E30")])],"isStart":false});
            var Q32;
            {var subQ0=sQuery(id+"F6.wireOp",EDGE,"E31");var subQ1=sQuery(id+"F6.wireOp",EDGE,"E34");var subQ2=sQuery(id+"F6.wireOp",EDGE,"E17");Q32=makeQuery(id+"F10.boolean.opBoolean","SPLIT",EDGE,{"disambiguationData":[TD([makeQuery(id+"F10.opExtrude","SWEPT_FACE",FACE,{"disambiguationData":[OSD([sQuery(id+"F9.wireOp",EDGE,"E43.right")])]})])],"derivedFrom":makeQuery(id+"F8.boolean.opBoolean","MERGE",EDGE,{"derivedFrom":[makeQuery(id+"F7.opExtrude","SWEPT_EDGE",EDGE,{"disambiguationData":[OSD([subQ2,subQ0,subQ1])]}),makeQuery(id+"F8.opExtrude","SWEPT_EDGE",EDGE,{"disambiguationData":[OSD([subQ2,subQ0,subQ1])]})]})});}
            var Q33;
            Q33=makeQuery(id+"F8.opExtrude","CAP_EDGE",EDGE,{"disambiguationData":[OSD([sQuery(id+"F6.wireOp",EDGE,"E34")])],"isStart":false});
            var Q34;
            {var subQ0=sQuery(id+"F6.wireOp",EDGE,"E34");var subQ1=sQuery(id+"F6.wireOp",EDGE,"E33");var subQ2=sQuery(id+"F6.wireOp",EDGE,"E17");Q34=makeQuery(id+"F10.boolean.opBoolean","SPLIT",EDGE,{"disambiguationData":[TD([makeQuery(id+"F10.opExtrude","SWEPT_FACE",FACE,{"disambiguationData":[OSD([sQuery(id+"F9.wireOp",EDGE,"E43.right")])]})])],"derivedFrom":makeQuery(id+"F8.boolean.opBoolean","MERGE",EDGE,{"derivedFrom":[makeQuery(id+"F7.opExtrude","SWEPT_EDGE",EDGE,{"disambiguationData":[OSD([subQ2,subQ1,subQ0])]}),makeQuery(id+"F8.opExtrude","SWEPT_EDGE",EDGE,{"disambiguationData":[OSD([subQ2,subQ1,subQ0])]})]})});}
            var Q35;
            {var subQ0=sQuery(id+"F6.wireOp",EDGE,"E34");var subQ1=sQuery(id+"F6.wireOp",EDGE,"E31");var subQ2=sQuery(id+"F6.wireOp",EDGE,"E17");Q35=makeQuery(id+"F10.boolean.opBoolean","SPLIT",EDGE,{"disambiguationData":[TD([makeQuery(id+"F10.opExtrude","SWEPT_FACE",FACE,{"disambiguationData":[OSD([sQuery(id+"F9.wireOp",EDGE,"E43.left")])]})])],"derivedFrom":makeQuery(id+"F8.boolean.opBoolean","MERGE",EDGE,{"derivedFrom":[makeQuery(id+"F7.opExtrude","SWEPT_EDGE",EDGE,{"disambiguationData":[OSD([subQ2,subQ1,subQ0])]}),makeQuery(id+"F8.opExtrude","SWEPT_EDGE",EDGE,{"disambiguationData":[OSD([subQ2,subQ1,subQ0])]})]})});}
            var Q36;
            {var subQ0=sQuery(id+"F6.wireOp",EDGE,"E34");var subQ1=sQuery(id+"F6.wireOp",EDGE,"E33");var subQ2=sQuery(id+"F6.wireOp",EDGE,"E17");Q36=makeQuery(id+"F10.boolean.opBoolean","SPLIT",EDGE,{"disambiguationData":[TD([makeQuery(id+"F10.opExtrude","SWEPT_FACE",FACE,{"disambiguationData":[OSD([sQuery(id+"F9.wireOp",EDGE,"E43.left")])]})])],"derivedFrom":makeQuery(id+"F8.boolean.opBoolean","MERGE",EDGE,{"derivedFrom":[makeQuery(id+"F7.opExtrude","SWEPT_EDGE",EDGE,{"disambiguationData":[OSD([subQ2,subQ1,subQ0])]}),makeQuery(id+"F8.opExtrude","SWEPT_EDGE",EDGE,{"disambiguationData":[OSD([subQ2,subQ1,subQ0])]})]})});}
            var Q37;
            Q37=makeQuery(id+"F7.opExtrude","CAP_EDGE",EDGE,{"disambiguationData":[OSD([sQuery(id+"F6.wireOp",EDGE,"E34")])],"isStart":false});
            var Q38;
            {var subQ0=sQuery(id+"F6.wireOp",EDGE,"E42");var subQ1=sQuery(id+"F6.wireOp",EDGE,"E39");var subQ2=sQuery(id+"F6.wireOp",EDGE,"E17");Q38=makeQuery(id+"F10.boolean.opBoolean","SPLIT",EDGE,{"disambiguationData":[TD([makeQuery(id+"F10.opExtrude","SWEPT_FACE",FACE,{"disambiguationData":[OSD([sQuery(id+"F9.wireOp",EDGE,"E43.right")])]})])],"derivedFrom":makeQuery(id+"F8.boolean.opBoolean","MERGE",EDGE,{"derivedFrom":[makeQuery(id+"F7.opExtrude","SWEPT_EDGE",EDGE,{"disambiguationData":[OSD([subQ2,subQ1,subQ0])]}),makeQuery(id+"F8.opExtrude","SWEPT_EDGE",EDGE,{"disambiguationData":[OSD([subQ2,subQ1,subQ0])]})]})});}
            var Q39;
            Q39=makeQuery(id+"F8.opExtrude","CAP_EDGE",EDGE,{"disambiguationData":[OSD([sQuery(id+"F6.wireOp",EDGE,"E39")])],"isStart":false});
            var Q40;
            {var subQ0=sQuery(id+"F6.wireOp",EDGE,"E39");var subQ1=sQuery(id+"F6.wireOp",EDGE,"E40");var subQ2=sQuery(id+"F6.wireOp",EDGE,"E17");Q40=makeQuery(id+"F10.boolean.opBoolean","SPLIT",EDGE,{"disambiguationData":[TD([makeQuery(id+"F10.opExtrude","SWEPT_FACE",FACE,{"disambiguationData":[OSD([sQuery(id+"F9.wireOp",EDGE,"E43.right")])]})])],"derivedFrom":makeQuery(id+"F8.boolean.opBoolean","MERGE",EDGE,{"derivedFrom":[makeQuery(id+"F7.opExtrude","SWEPT_EDGE",EDGE,{"disambiguationData":[OSD([subQ2,subQ0,subQ1])]}),makeQuery(id+"F8.opExtrude","SWEPT_EDGE",EDGE,{"disambiguationData":[OSD([subQ2,subQ0,subQ1])]})]})});}
            var Q41;
            {var subQ0=sQuery(id+"F6.wireOp",EDGE,"E40");var subQ1=sQuery(id+"F6.wireOp",EDGE,"E39");var subQ2=sQuery(id+"F6.wireOp",EDGE,"E17");Q41=makeQuery(id+"F10.boolean.opBoolean","SPLIT",EDGE,{"disambiguationData":[TD([makeQuery(id+"F10.opExtrude","SWEPT_FACE",FACE,{"disambiguationData":[OSD([sQuery(id+"F9.wireOp",EDGE,"E43.left")])]})])],"derivedFrom":makeQuery(id+"F8.boolean.opBoolean","MERGE",EDGE,{"derivedFrom":[makeQuery(id+"F7.opExtrude","SWEPT_EDGE",EDGE,{"disambiguationData":[OSD([subQ2,subQ1,subQ0])]}),makeQuery(id+"F8.opExtrude","SWEPT_EDGE",EDGE,{"disambiguationData":[OSD([subQ2,subQ1,subQ0])]})]})});}
            var Q42;
            {var subQ0=sQuery(id+"F6.wireOp",EDGE,"E39");var subQ1=sQuery(id+"F6.wireOp",EDGE,"E42");var subQ2=sQuery(id+"F6.wireOp",EDGE,"E17");Q42=makeQuery(id+"F10.boolean.opBoolean","SPLIT",EDGE,{"disambiguationData":[TD([makeQuery(id+"F10.opExtrude","SWEPT_FACE",FACE,{"disambiguationData":[OSD([sQuery(id+"F9.wireOp",EDGE,"E43.left")])]})])],"derivedFrom":makeQuery(id+"F8.boolean.opBoolean","MERGE",EDGE,{"derivedFrom":[makeQuery(id+"F7.opExtrude","SWEPT_EDGE",EDGE,{"disambiguationData":[OSD([subQ2,subQ0,subQ1])]}),makeQuery(id+"F8.opExtrude","SWEPT_EDGE",EDGE,{"disambiguationData":[OSD([subQ2,subQ0,subQ1])]})]})});}
            var Q43;
            Q43=makeQuery(id+"F7.opExtrude","CAP_EDGE",EDGE,{"disambiguationData":[OSD([sQuery(id+"F6.wireOp",EDGE,"E39")])],"isStart":false});
            fillet(context, id + "F11", {"entities" : qUnion([Q0, Q1, Q2, Q3, Q4, Q5, Q6, Q7, Q8, Q9, Q10, Q11, Q12, Q13, Q14, Q15, Q16, Q17, Q18, Q19, Q20, Q21, Q22, Q23, Q24, Q25, Q26, Q27, Q28, Q29, Q30, Q31, Q32, Q33, Q34, Q35, Q36, Q37, Q38, Q39, Q40, Q41, Q42, Q43]), "radius" : 0.25 * mm, "tangentPropagation" : true, "allowEdgeOverflow" : false});
        }
        {
            var Q0;
            Q0=makeQuery(id+"F10.opExtrude","CAP_EDGE",EDGE,{"disambiguationData":[OSD([sQuery(id+"F9.wireOp",EDGE,"E43.bottom")])],"isStart":true});
            var Q1;
            Q1=makeQuery(id+"F10.opExtrude","CAP_EDGE",EDGE,{"disambiguationData":[OSD([sQuery(id+"F9.wireOp",EDGE,"E43.top")])],"isStart":true});
            chamfer(context, id + "F12", {"entities" : qUnion([Q0, Q1]), "chamferType" : ChamferType.OFFSET_ANGLE, "width" : 8.38 * mm, "oppositeDirection" : true, "angle" : 11 * degree, "tangentPropagation" : true});
        }
        {
            var Q0;
            {var subQ0=sQuery(id+"F6.wireOp",EDGE,"E18.left");Q0=makeQuery(id+"F10.boolean.opBoolean","MERGE",FACE,{"derivedFrom":[makeQuery(id+"F8.boolean.opBoolean","MERGE",FACE,{"derivedFrom":[makeQuery(id+"F7.opExtrude","SWEPT_FACE",FACE,{"disambiguationData":[OSD([subQ0])]}),makeQuery(id+"F8.opExtrude","SWEPT_FACE",FACE,{"disambiguationData":[OSD([subQ0])]})]}),makeQuery(id+"F10.opExtrude","CAP_FACE",FACE,{"disambiguationData":[OSD([sQuery(id+"F9.wireOp",EDGE,"E43.bottom"),sQuery(id+"F9.wireOp",EDGE,"E43.top"),sQuery(id+"F9.wireOp",EDGE,"E43.left"),sQuery(id+"F9.wireOp",EDGE,"E43.right")])],"isStart":true})]});}
            var sketch = newSketch(context, id + "F13", { "sketchPlane" : qUnion([Q0])});
            skLineSegment(sketch, "E44", {"start": v(1.78, 32.26) * mm, "end": v(1.78, 31.24) * mm});
            skLineSegment(sketch, "E45", {"start": v(3.3, 32.26) * mm, "end": v(3.3, 31.24) * mm});
            skLineSegment(sketch, "E46", {"start": v(3.3, 31.24) * mm, "end": v(3.3, 27.43) * mm});
            skLineSegment(sketch, "E47", {"start": v(3.3, 27.43) * mm, "end": v(1.78, 27.43) * mm});
            skLineSegment(sketch, "E48", {"start": v(1.78, 27.43) * mm, "end": v(1.78, 31.24) * mm});
            skLineSegment(sketch, "E49", {"start": v(1.78, 32.26) * mm, "end": v(1.78, 36.07) * mm});
            skLineSegment(sketch, "E50", {"start": v(1.78, 36.07) * mm, "end": v(3.3, 36.07) * mm});
            skLineSegment(sketch, "E51", {"start": v(3.3, 36.07) * mm, "end": v(3.3, 32.26) * mm});
            skSolve(sketch);
        }
        {
            var Q0;
            Q0=makeQuery(id+"F13.imprint","IMPRINT",FACE,{"disambiguationData":[TD([[makeQuery(id+"F13.imprint","IMPRINT",EDGE,{"derivedFrom":sQuery(id+"F13.wireOp",EDGE,"E44")}),1.0]])]});
            extrude(context, id + "F14", {"entities" : qUnion([Q0]), "operationType" : NewBodyOperationType.REMOVE, "oppositeDirection" : true, "depth" : 0.25 * mm});
        }
        {
            var Q0;
            Q0=makeQuery(id+"F12.opChamfer","BLEND_FACE",FACE,{"disambiguationData":[OSD([sQuery(id+"F9.wireOp",EDGE,"E43.top")])]});
            var Q1;
            Q1=makeQuery(id+"F12.opChamfer","BLEND_FACE",FACE,{"disambiguationData":[OSD([sQuery(id+"F9.wireOp",EDGE,"E43.bottom")])]});
            extrude(context, id + "F15", {"entities" : qUnion([Q0, Q1]), "operationType" : NewBodyOperationType.REMOVE, "oppositeDirection" : true, "depth" : 0.25 * mm});
        }
        {
            var Q0;
            Q0=makeQuery(id+"F15.boolean.opBoolean","COPY",FACE,{"derivedFrom":makeQuery(id+"F15.opExtrude","SWEPT_FACE",FACE,{"disambiguationData":[OSD([sQuery(id+"F6.wireOp",EDGE,"E18.left"),sQuery(id+"F9.wireOp",EDGE,"E43.bottom"),sQuery(id+"F9.wireOp",EDGE,"E43.top"),sQuery(id+"F9.wireOp",EDGE,"E43.left"),sQuery(id+"F9.wireOp",EDGE,"E43.right"),sQuery(id+"F13.wireOp",EDGE,"E47")])]})});
            extrude(context, id + "F16", {"entities" : qUnion([Q0]), "operationType" : NewBodyOperationType.REMOVE, "oppositeDirection" : true, "depth" : 0.05 * mm});
        }
        {
            var Q0;
            Q0=makeQuery(id+"F15.boolean.opBoolean","COPY",FACE,{"derivedFrom":makeQuery(id+"F15.opExtrude","SWEPT_FACE",FACE,{"disambiguationData":[OSD([sQuery(id+"F9.wireOp",EDGE,"E43.top")])]})});
            extrude(context, id + "F17", {"entities" : qUnion([Q0]), "operationType" : NewBodyOperationType.REMOVE, "oppositeDirection" : true, "depth" : 0.05 * mm});
        }
        {
            var Q0;
            {var subQ0=sQuery(id+"F9.wireOp",EDGE,"E43.left");var subQ2=sQuery(id+"F6.wireOp",EDGE,"E39");var subQ4=makeQuery(id+"F7.opExtrude","SWEPT_FACE",FACE,{"disambiguationData":[OSD([subQ2])]});var subQ9=sQuery(id+"F9.wireOp",EDGE,"E43.bottom");Q0=makeQuery(id+"F15.boolean.opBoolean","COPY",FACE,{"disambiguationData":[TD([subQ4])],"derivedFrom":makeQuery(id+"F15.opExtrude","SWEPT_FACE",FACE,{"disambiguationData":[OSD([subQ9,subQ0])]})});}
            var Q1;
            {var subQ0=sQuery(id+"F6.wireOp",EDGE,"E34");var subQ5=makeQuery(id+"F7.opExtrude","SWEPT_FACE",FACE,{"disambiguationData":[OSD([subQ0])]});var subQ6=sQuery(id+"F9.wireOp",EDGE,"E43.left");var subQ9=sQuery(id+"F9.wireOp",EDGE,"E43.bottom");Q1=makeQuery(id+"F15.boolean.opBoolean","COPY",FACE,{"disambiguationData":[TD([subQ5])],"derivedFrom":makeQuery(id+"F15.opExtrude","SWEPT_FACE",FACE,{"disambiguationData":[OSD([subQ9,subQ6])]})});}
            var Q2;
            {var subQ0=sQuery(id+"F6.wireOp",EDGE,"E30");var subQ5=makeQuery(id+"F7.opExtrude","SWEPT_FACE",FACE,{"disambiguationData":[OSD([subQ0])]});var subQ8=sQuery(id+"F13.wireOp",EDGE,"E51");var subQ9=sQuery(id+"F13.wireOp",EDGE,"E46");var subQ10=sQuery(id+"F13.wireOp",EDGE,"E45");Q2=makeQuery(id+"F14.boolean.opBoolean","COPY",FACE,{"disambiguationData":[TD([subQ5])],"derivedFrom":makeQuery(id+"F14.opExtrude","SWEPT_FACE",FACE,{"disambiguationData":[OSD([subQ10,subQ9,subQ8])]})});}
            var Q3;
            {var subQ8=sQuery(id+"F6.wireOp",EDGE,"E18.bottom");var subQ13=makeQuery(id+"F7.opExtrude","SWEPT_FACE",FACE,{"disambiguationData":[OSD([subQ8])]});var subQ14=sQuery(id+"F13.wireOp",EDGE,"E51");var subQ15=sQuery(id+"F13.wireOp",EDGE,"E46");var subQ16=sQuery(id+"F13.wireOp",EDGE,"E45");Q3=makeQuery(id+"F14.boolean.opBoolean","COPY",FACE,{"disambiguationData":[TD([subQ13])],"derivedFrom":makeQuery(id+"F14.opExtrude","SWEPT_FACE",FACE,{"disambiguationData":[OSD([subQ16,subQ15,subQ14])]})});}
            var Q4;
            {var subQ0=sQuery(id+"F6.wireOp",EDGE,"E21");var subQ2=makeQuery(id+"F7.opExtrude","SWEPT_FACE",FACE,{"disambiguationData":[OSD([subQ0])]});var subQ8=sQuery(id+"F13.wireOp",EDGE,"E51");var subQ9=sQuery(id+"F13.wireOp",EDGE,"E46");var subQ10=sQuery(id+"F13.wireOp",EDGE,"E45");Q4=makeQuery(id+"F14.boolean.opBoolean","COPY",FACE,{"disambiguationData":[TD([subQ2])],"derivedFrom":makeQuery(id+"F14.opExtrude","SWEPT_FACE",FACE,{"disambiguationData":[OSD([subQ10,subQ9,subQ8])]})});}
            var Q5;
            {var subQ1=sQuery(id+"F6.wireOp",EDGE,"E23");var subQ3=makeQuery(id+"F7.opExtrude","SWEPT_FACE",FACE,{"disambiguationData":[OSD([subQ1])]});var subQ7=sQuery(id+"F9.wireOp",EDGE,"E43.left");var subQ9=sQuery(id+"F9.wireOp",EDGE,"E43.top");Q5=makeQuery(id+"F15.boolean.opBoolean","COPY",FACE,{"disambiguationData":[TD([subQ3])],"derivedFrom":makeQuery(id+"F15.opExtrude","SWEPT_FACE",FACE,{"disambiguationData":[OSD([subQ9,subQ7])]})});}
            var Q6;
            {var subQ0=sQuery(id+"F6.wireOp",EDGE,"E35");var subQ5=makeQuery(id+"F7.opExtrude","SWEPT_FACE",FACE,{"disambiguationData":[OSD([subQ0])]});var subQ6=sQuery(id+"F9.wireOp",EDGE,"E43.left");var subQ9=sQuery(id+"F9.wireOp",EDGE,"E43.top");Q6=makeQuery(id+"F15.boolean.opBoolean","COPY",FACE,{"disambiguationData":[TD([subQ5])],"derivedFrom":makeQuery(id+"F15.opExtrude","SWEPT_FACE",FACE,{"disambiguationData":[OSD([subQ9,subQ6])]})});}
            extrude(context, id + "F18", {"entities" : qUnion([Q0, Q1, Q2, Q3, Q4, Q5, Q6]), "operationType" : NewBodyOperationType.ADD, "depth" : 5.08 * mm});
        }
        {
            var Q0;
            {var subQ0=sQuery(id+"F9.wireOp",EDGE,"E43.left");var subQ1=sQuery(id+"F9.wireOp",EDGE,"E43.bottom");var subQ2=makeQuery(id+"F10.opExtrude","SWEPT_FACE",FACE,{"disambiguationData":[OSD([subQ0])]});var subQ6=makeQuery(id+"F15.opExtrude","CAP_FACE",FACE,{"disambiguationData":[OSD([subQ1]),OD(1.0)],"isStart":false});Q0=makeQuery(id+"F15.boolean.opBoolean","COPY",EDGE,{"disambiguationData":[topologyDisambiguationEdgeConnected([subQ2,subQ6]),TD([makeQuery(id+"F10.opExtrude","SWEPT_FACE",FACE,{"disambiguationData":[OSD([subQ1])]})])],"derivedFrom":makeQuery(id+"F15.opExtrude","CAP_EDGE",EDGE,{"disambiguationData":[OSD([subQ1,subQ0]),OD(1.0)],"isStart":false})});}
            var Q1;
            {var subQ0=sQuery(id+"F9.wireOp",EDGE,"E43.bottom");Q1=makeQuery(id+"F15.boolean.opBoolean","INTERSECT",EDGE,{"derivedFrom":[makeQuery(id+"F10.opExtrude","SWEPT_FACE",FACE,{"disambiguationData":[OSD([subQ0])]}),makeQuery(id+"F15.opExtrude","CAP_FACE",FACE,{"disambiguationData":[OSD([subQ0]),OD(1.0)],"isStart":false})]});}
            var Q2;
            {var subQ2=sQuery(id+"F9.wireOp",EDGE,"E43.right");var subQ3=makeQuery(id+"F10.opExtrude","SWEPT_FACE",FACE,{"disambiguationData":[OSD([subQ2])]});var subQ5=sQuery(id+"F9.wireOp",EDGE,"E43.bottom");var subQ6=makeQuery(id+"F15.opExtrude","CAP_FACE",FACE,{"disambiguationData":[OSD([subQ5]),OD(1.0)],"isStart":false});Q2=makeQuery(id+"F15.boolean.opBoolean","COPY",EDGE,{"disambiguationData":[topologyDisambiguationEdgeConnected([subQ3,subQ6]),TD([makeQuery(id+"F10.opExtrude","SWEPT_FACE",FACE,{"disambiguationData":[OSD([subQ5])]})])],"derivedFrom":makeQuery(id+"F15.opExtrude","CAP_EDGE",EDGE,{"disambiguationData":[OSD([subQ5,subQ2]),OD(1.0)],"isStart":false})});}
            var Q3;
            {var subQ1=sQuery(id+"F9.wireOp",EDGE,"E43.right");var subQ2=makeQuery(id+"F10.opExtrude","SWEPT_FACE",FACE,{"disambiguationData":[OSD([subQ1])]});var subQ4=sQuery(id+"F6.wireOp",EDGE,"E17");var subQ5=sQuery(id+"F9.wireOp",EDGE,"E43.bottom");var subQ6=sQuery(id+"F6.wireOp",EDGE,"E34");var subQ7=sQuery(id+"F6.wireOp",EDGE,"E33");var subQ8=makeQuery(id+"F15.opExtrude","CAP_FACE",FACE,{"disambiguationData":[OSD([subQ5]),OD(1.0)],"isStart":false});Q3=makeQuery(id+"F15.boolean.opBoolean","COPY",EDGE,{"disambiguationData":[topologyDisambiguationEdgeConnected([subQ2,subQ8]),TD([makeQuery(id+"F11.opFillet","BLEND_FACE",FACE,{"disambiguationData":[OSD([subQ4,subQ7,subQ6]),TDD([makeQuery(id+"F10.boolean.opBoolean","SPLIT",EDGE,{"disambiguationData":[TD([subQ2])],"derivedFrom":makeQuery(id+"F8.boolean.opBoolean","MERGE",EDGE,{"derivedFrom":[makeQuery(id+"F7.opExtrude","SWEPT_EDGE",EDGE,{"disambiguationData":[OSD([subQ4,subQ7,subQ6])]}),makeQuery(id+"F8.opExtrude","SWEPT_EDGE",EDGE,{"disambiguationData":[OSD([subQ4,subQ7,subQ6])]})]})})])]})])],"derivedFrom":makeQuery(id+"F15.opExtrude","CAP_EDGE",EDGE,{"disambiguationData":[OSD([subQ5,subQ1]),OD(1.0)],"isStart":false})});}
            var Q4;
            {var subQ2=sQuery(id+"F9.wireOp",EDGE,"E43.left");var subQ3=makeQuery(id+"F10.opExtrude","SWEPT_FACE",FACE,{"disambiguationData":[OSD([subQ2])]});var subQ4=sQuery(id+"F6.wireOp",EDGE,"E17");var subQ5=sQuery(id+"F9.wireOp",EDGE,"E43.bottom");var subQ6=sQuery(id+"F6.wireOp",EDGE,"E34");var subQ7=sQuery(id+"F6.wireOp",EDGE,"E33");var subQ8=makeQuery(id+"F15.opExtrude","CAP_FACE",FACE,{"disambiguationData":[OSD([subQ5]),OD(1.0)],"isStart":false});Q4=makeQuery(id+"F15.boolean.opBoolean","COPY",EDGE,{"disambiguationData":[topologyDisambiguationEdgeConnected([subQ3,subQ8]),TD([makeQuery(id+"F11.opFillet","BLEND_FACE",FACE,{"disambiguationData":[OSD([subQ4,subQ7,subQ6]),TDD([makeQuery(id+"F10.boolean.opBoolean","SPLIT",EDGE,{"disambiguationData":[TD([subQ3])],"derivedFrom":makeQuery(id+"F8.boolean.opBoolean","MERGE",EDGE,{"derivedFrom":[makeQuery(id+"F7.opExtrude","SWEPT_EDGE",EDGE,{"disambiguationData":[OSD([subQ4,subQ7,subQ6])]}),makeQuery(id+"F8.opExtrude","SWEPT_EDGE",EDGE,{"disambiguationData":[OSD([subQ4,subQ7,subQ6])]})]})})])]})])],"derivedFrom":makeQuery(id+"F15.opExtrude","CAP_EDGE",EDGE,{"disambiguationData":[OSD([subQ5,subQ2]),OD(1.0)],"isStart":false})});}
            var Q5;
            {var subQ0=sQuery(id+"F9.wireOp",EDGE,"E43.right");var subQ1=sQuery(id+"F9.wireOp",EDGE,"E43.bottom");var subQ4=makeQuery(id+"F10.opExtrude","SWEPT_FACE",FACE,{"disambiguationData":[OSD([subQ0])]});var subQ6=makeQuery(id+"F15.opExtrude","CAP_FACE",FACE,{"disambiguationData":[OSD([subQ1]),OD(1.0)],"isStart":false});Q5=makeQuery(id+"F15.boolean.opBoolean","COPY",EDGE,{"disambiguationData":[topologyDisambiguationEdgeConnected([subQ4,subQ6]),TD([makeQuery(id+"F15.opExtrude","SWEPT_FACE",FACE,{"disambiguationData":[OSD([sQuery(id+"F6.wireOp",EDGE,"E18.left"),subQ1,sQuery(id+"F9.wireOp",EDGE,"E43.top"),sQuery(id+"F9.wireOp",EDGE,"E43.left"),subQ0,sQuery(id+"F13.wireOp",EDGE,"E47")])]})])],"derivedFrom":makeQuery(id+"F15.opExtrude","CAP_EDGE",EDGE,{"disambiguationData":[OSD([subQ1,subQ0]),OD(1.0)],"isStart":false})});}
            var Q6;
            {var subQ0=sQuery(id+"F9.wireOp",EDGE,"E43.left");var subQ1=sQuery(id+"F9.wireOp",EDGE,"E43.bottom");var subQ4=makeQuery(id+"F10.opExtrude","SWEPT_FACE",FACE,{"disambiguationData":[OSD([subQ0])]});var subQ6=makeQuery(id+"F15.opExtrude","CAP_FACE",FACE,{"disambiguationData":[OSD([subQ1]),OD(1.0)],"isStart":false});Q6=makeQuery(id+"F15.boolean.opBoolean","COPY",EDGE,{"disambiguationData":[topologyDisambiguationEdgeConnected([subQ4,subQ6]),TD([makeQuery(id+"F15.opExtrude","SWEPT_FACE",FACE,{"disambiguationData":[OSD([sQuery(id+"F6.wireOp",EDGE,"E18.left"),subQ1,sQuery(id+"F9.wireOp",EDGE,"E43.top"),subQ0,sQuery(id+"F9.wireOp",EDGE,"E43.right"),sQuery(id+"F13.wireOp",EDGE,"E47")])]})])],"derivedFrom":makeQuery(id+"F15.opExtrude","CAP_EDGE",EDGE,{"disambiguationData":[OSD([subQ1,subQ0]),OD(1.0)],"isStart":false})});}
            var Q7;
            {var subQ1=sQuery(id+"F6.wireOp",EDGE,"E18.top");var subQ2=sQuery(id+"F9.wireOp",EDGE,"E43.right");var subQ3=makeQuery(id+"F10.opExtrude","SWEPT_FACE",FACE,{"disambiguationData":[OSD([subQ2])]});var subQ5=makeQuery(id+"F7.opExtrude","SWEPT_FACE",FACE,{"disambiguationData":[OSD([subQ1])]});var subQ7=sQuery(id+"F13.wireOp",EDGE,"E49");var subQ8=sQuery(id+"F13.wireOp",EDGE,"E48");var subQ9=sQuery(id+"F13.wireOp",EDGE,"E44");var subQ10=makeQuery(id+"F14.opExtrude","CAP_FACE",FACE,{"disambiguationData":[OSD([subQ9,sQuery(id+"F13.wireOp",EDGE,"E45"),sQuery(id+"F13.wireOp",EDGE,"E46"),sQuery(id+"F13.wireOp",EDGE,"E47"),subQ8,subQ7,sQuery(id+"F13.wireOp",EDGE,"E50"),sQuery(id+"F13.wireOp",EDGE,"E51")])],"isStart":false});Q7=makeQuery(id+"F14.boolean.opBoolean","COPY",EDGE,{"disambiguationData":[topologyDisambiguationEdgeConnected([subQ3,subQ10]),TD([subQ5])],"derivedFrom":makeQuery(id+"F14.opExtrude","CAP_EDGE",EDGE,{"disambiguationData":[OSD([subQ9,subQ8,subQ7])],"isStart":false})});}
            var Q8;
            {var subQ1=sQuery(id+"F6.wireOp",EDGE,"E18.top");var subQ2=makeQuery(id+"F7.opExtrude","SWEPT_FACE",FACE,{"disambiguationData":[OSD([subQ1])]});var subQ4=sQuery(id+"F9.wireOp",EDGE,"E43.left");var subQ5=makeQuery(id+"F10.opExtrude","SWEPT_FACE",FACE,{"disambiguationData":[OSD([subQ4])]});var subQ9=sQuery(id+"F13.wireOp",EDGE,"E51");var subQ10=sQuery(id+"F13.wireOp",EDGE,"E46");var subQ11=sQuery(id+"F13.wireOp",EDGE,"E45");var subQ12=makeQuery(id+"F14.opExtrude","CAP_FACE",FACE,{"disambiguationData":[OSD([sQuery(id+"F13.wireOp",EDGE,"E44"),subQ11,subQ10,sQuery(id+"F13.wireOp",EDGE,"E47"),sQuery(id+"F13.wireOp",EDGE,"E48"),sQuery(id+"F13.wireOp",EDGE,"E49"),sQuery(id+"F13.wireOp",EDGE,"E50"),subQ9])],"isStart":false});Q8=makeQuery(id+"F14.boolean.opBoolean","COPY",EDGE,{"disambiguationData":[topologyDisambiguationEdgeConnected([subQ5,subQ12]),TD([subQ2])],"derivedFrom":makeQuery(id+"F14.opExtrude","CAP_EDGE",EDGE,{"disambiguationData":[OSD([subQ11,subQ10,subQ9])],"isStart":false})});}
            var Q9;
            {var subQ1=sQuery(id+"F6.wireOp",EDGE,"E18.bottom");var subQ3=makeQuery(id+"F7.opExtrude","SWEPT_FACE",FACE,{"disambiguationData":[OSD([subQ1])]});var subQ4=sQuery(id+"F9.wireOp",EDGE,"E43.left");var subQ5=makeQuery(id+"F10.opExtrude","SWEPT_FACE",FACE,{"disambiguationData":[OSD([subQ4])]});var subQ7=sQuery(id+"F13.wireOp",EDGE,"E51");var subQ8=sQuery(id+"F13.wireOp",EDGE,"E46");var subQ9=sQuery(id+"F13.wireOp",EDGE,"E45");var subQ10=makeQuery(id+"F14.opExtrude","CAP_FACE",FACE,{"disambiguationData":[OSD([sQuery(id+"F13.wireOp",EDGE,"E44"),subQ9,subQ8,sQuery(id+"F13.wireOp",EDGE,"E47"),sQuery(id+"F13.wireOp",EDGE,"E48"),sQuery(id+"F13.wireOp",EDGE,"E49"),sQuery(id+"F13.wireOp",EDGE,"E50"),subQ7])],"isStart":false});Q9=makeQuery(id+"F14.boolean.opBoolean","COPY",EDGE,{"disambiguationData":[topologyDisambiguationEdgeConnected([subQ5,subQ10]),TD([subQ3])],"derivedFrom":makeQuery(id+"F14.opExtrude","CAP_EDGE",EDGE,{"disambiguationData":[OSD([subQ9,subQ8,subQ7])],"isStart":false})});}
            var Q10;
            {var subQ0=sQuery(id+"F9.wireOp",EDGE,"E43.right");var subQ1=makeQuery(id+"F10.opExtrude","SWEPT_FACE",FACE,{"disambiguationData":[OSD([subQ0])]});var subQ2=sQuery(id+"F6.wireOp",EDGE,"E18.bottom");var subQ4=sQuery(id+"F13.wireOp",EDGE,"E49");var subQ5=sQuery(id+"F13.wireOp",EDGE,"E48");var subQ6=sQuery(id+"F13.wireOp",EDGE,"E44");var subQ7=makeQuery(id+"F14.opExtrude","CAP_FACE",FACE,{"disambiguationData":[OSD([subQ6,sQuery(id+"F13.wireOp",EDGE,"E45"),sQuery(id+"F13.wireOp",EDGE,"E46"),sQuery(id+"F13.wireOp",EDGE,"E47"),subQ5,subQ4,sQuery(id+"F13.wireOp",EDGE,"E50"),sQuery(id+"F13.wireOp",EDGE,"E51")])],"isStart":false});var subQ9=makeQuery(id+"F7.opExtrude","SWEPT_FACE",FACE,{"disambiguationData":[OSD([subQ2])]});Q10=makeQuery(id+"F14.boolean.opBoolean","COPY",EDGE,{"disambiguationData":[topologyDisambiguationEdgeConnected([subQ1,subQ7]),TD([subQ9])],"derivedFrom":makeQuery(id+"F14.opExtrude","CAP_EDGE",EDGE,{"disambiguationData":[OSD([subQ6,subQ5,subQ4])],"isStart":false})});}
            var Q11;
            {var subQ0=sQuery(id+"F9.wireOp",EDGE,"E43.right");var subQ1=sQuery(id+"F9.wireOp",EDGE,"E43.top");var subQ2=makeQuery(id+"F15.opExtrude","CAP_FACE",FACE,{"disambiguationData":[OSD([subQ1])],"isStart":false});var subQ3=sQuery(id+"F6.wireOp",EDGE,"E26");var subQ4=makeQuery(id+"F10.opExtrude","SWEPT_FACE",FACE,{"disambiguationData":[OSD([subQ0])]});var subQ5=sQuery(id+"F6.wireOp",EDGE,"E23");var subQ6=sQuery(id+"F6.wireOp",EDGE,"E17");Q11=makeQuery(id+"F15.boolean.opBoolean","COPY",EDGE,{"disambiguationData":[topologyDisambiguationEdgeConnected([subQ4,subQ2]),TD([makeQuery(id+"F11.opFillet","BLEND_FACE",FACE,{"disambiguationData":[OSD([subQ6,subQ5,subQ3]),TDD([makeQuery(id+"F10.boolean.opBoolean","SPLIT",EDGE,{"disambiguationData":[TD([subQ4])],"derivedFrom":makeQuery(id+"F8.boolean.opBoolean","MERGE",EDGE,{"derivedFrom":[makeQuery(id+"F7.opExtrude","SWEPT_EDGE",EDGE,{"disambiguationData":[OSD([subQ6,subQ5,subQ3])]}),makeQuery(id+"F8.opExtrude","SWEPT_EDGE",EDGE,{"disambiguationData":[OSD([subQ6,subQ5,subQ3])]})]})})])]})])],"derivedFrom":makeQuery(id+"F15.opExtrude","CAP_EDGE",EDGE,{"disambiguationData":[OSD([subQ1,subQ0])],"isStart":false})});}
            var Q12;
            {var subQ0=sQuery(id+"F9.wireOp",EDGE,"E43.left");var subQ1=sQuery(id+"F9.wireOp",EDGE,"E43.top");var subQ2=makeQuery(id+"F15.opExtrude","CAP_FACE",FACE,{"disambiguationData":[OSD([subQ1])],"isStart":false});var subQ3=sQuery(id+"F6.wireOp",EDGE,"E26");var subQ4=sQuery(id+"F6.wireOp",EDGE,"E23");var subQ5=sQuery(id+"F6.wireOp",EDGE,"E17");var subQ6=makeQuery(id+"F10.opExtrude","SWEPT_FACE",FACE,{"disambiguationData":[OSD([subQ0])]});Q12=makeQuery(id+"F15.boolean.opBoolean","COPY",EDGE,{"disambiguationData":[topologyDisambiguationEdgeConnected([subQ6,subQ2]),TD([makeQuery(id+"F11.opFillet","BLEND_FACE",FACE,{"disambiguationData":[OSD([subQ5,subQ4,subQ3]),TDD([makeQuery(id+"F10.boolean.opBoolean","SPLIT",EDGE,{"disambiguationData":[TD([subQ6])],"derivedFrom":makeQuery(id+"F8.boolean.opBoolean","MERGE",EDGE,{"derivedFrom":[makeQuery(id+"F7.opExtrude","SWEPT_EDGE",EDGE,{"disambiguationData":[OSD([subQ5,subQ4,subQ3])]}),makeQuery(id+"F8.opExtrude","SWEPT_EDGE",EDGE,{"disambiguationData":[OSD([subQ5,subQ4,subQ3])]})]})})])]})])],"derivedFrom":makeQuery(id+"F15.opExtrude","CAP_EDGE",EDGE,{"disambiguationData":[OSD([subQ1,subQ0])],"isStart":false})});}
            var Q13;
            {var subQ0=sQuery(id+"F9.wireOp",EDGE,"E43.left");var subQ1=sQuery(id+"F9.wireOp",EDGE,"E43.top");var subQ2=sQuery(id+"F6.wireOp",EDGE,"E24");var subQ3=sQuery(id+"F6.wireOp",EDGE,"E17");var subQ4=makeQuery(id+"F10.opExtrude","SWEPT_FACE",FACE,{"disambiguationData":[OSD([subQ0])]});var subQ7=makeQuery(id+"F15.opExtrude","CAP_FACE",FACE,{"disambiguationData":[OSD([subQ1])],"isStart":false});Q13=makeQuery(id+"F15.boolean.opBoolean","COPY",EDGE,{"disambiguationData":[topologyDisambiguationEdgeConnected([subQ4,subQ7]),TD([makeQuery(id+"F11.opFillet","BLEND_FACE",FACE,{"disambiguationData":[OSD([subQ3,subQ2]),TDD([makeQuery(id+"F10.boolean.opBoolean","SPLIT",EDGE,{"disambiguationData":[TD([subQ4])],"derivedFrom":makeQuery(id+"F8.boolean.opBoolean","MERGE",EDGE,{"derivedFrom":[makeQuery(id+"F7.opExtrude","SWEPT_EDGE",EDGE,{"disambiguationData":[OSD([subQ3,subQ2])]}),makeQuery(id+"F8.opExtrude","SWEPT_EDGE",EDGE,{"disambiguationData":[OSD([subQ3,subQ2])]})]})})])]})])],"derivedFrom":makeQuery(id+"F15.opExtrude","CAP_EDGE",EDGE,{"disambiguationData":[OSD([subQ1,subQ0])],"isStart":false})});}
            var Q14;
            {var subQ0=sQuery(id+"F9.wireOp",EDGE,"E43.right");var subQ1=sQuery(id+"F9.wireOp",EDGE,"E43.top");var subQ2=sQuery(id+"F6.wireOp",EDGE,"E24");var subQ3=sQuery(id+"F6.wireOp",EDGE,"E17");var subQ4=makeQuery(id+"F10.opExtrude","SWEPT_FACE",FACE,{"disambiguationData":[OSD([subQ0])]});var subQ7=makeQuery(id+"F15.opExtrude","CAP_FACE",FACE,{"disambiguationData":[OSD([subQ1])],"isStart":false});Q14=makeQuery(id+"F15.boolean.opBoolean","COPY",EDGE,{"disambiguationData":[topologyDisambiguationEdgeConnected([subQ4,subQ7]),TD([makeQuery(id+"F11.opFillet","BLEND_FACE",FACE,{"disambiguationData":[OSD([subQ3,subQ2]),TDD([makeQuery(id+"F10.boolean.opBoolean","SPLIT",EDGE,{"disambiguationData":[TD([subQ4])],"derivedFrom":makeQuery(id+"F8.boolean.opBoolean","MERGE",EDGE,{"derivedFrom":[makeQuery(id+"F7.opExtrude","SWEPT_EDGE",EDGE,{"disambiguationData":[OSD([subQ3,subQ2])]}),makeQuery(id+"F8.opExtrude","SWEPT_EDGE",EDGE,{"disambiguationData":[OSD([subQ3,subQ2])]})]})})])]})])],"derivedFrom":makeQuery(id+"F15.opExtrude","CAP_EDGE",EDGE,{"disambiguationData":[OSD([subQ1,subQ0])],"isStart":false})});}
            var Q15;
            {var subQ0=sQuery(id+"F9.wireOp",EDGE,"E43.right");var subQ1=sQuery(id+"F9.wireOp",EDGE,"E43.top");var subQ4=makeQuery(id+"F10.opExtrude","SWEPT_FACE",FACE,{"disambiguationData":[OSD([subQ0])]});var subQ6=makeQuery(id+"F15.opExtrude","CAP_FACE",FACE,{"disambiguationData":[OSD([subQ1])],"isStart":false});Q15=makeQuery(id+"F17.boolean.opBoolean","MERGE",EDGE,{"derivedFrom":[makeQuery(id+"F15.boolean.opBoolean","COPY",EDGE,{"disambiguationData":[topologyDisambiguationEdgeConnected([subQ4,subQ6]),TD([makeQuery(id+"F15.opExtrude","SWEPT_FACE",FACE,{"disambiguationData":[OSD([subQ1])]})])],"derivedFrom":makeQuery(id+"F15.opExtrude","CAP_EDGE",EDGE,{"disambiguationData":[OSD([subQ1,subQ0])],"isStart":false})}),makeQuery(id+"F17.opExtrude","SWEPT_EDGE",EDGE,{"disambiguationData":[OSD([subQ1,subQ0]),TDD([makeQuery(id+"F15.boolean.opBoolean","COPY",VERTEX,{"derivedFrom":makeQuery(id+"F15.opExtrude","CAP_VERTEX",VERTEX,{"disambiguationData":[OSD([subQ1,subQ0])],"isStart":false})})])]})]});}
            var Q16;
            {var subQ0=sQuery(id+"F9.wireOp",EDGE,"E43.top");Q16=makeQuery(id+"F17.boolean.opBoolean","INTERSECT",EDGE,{"derivedFrom":[makeQuery(id+"F10.opExtrude","SWEPT_FACE",FACE,{"disambiguationData":[OSD([subQ0])]}),makeQuery(id+"F17.opExtrude","SWEPT_FACE",FACE,{"disambiguationData":[OSD([subQ0]),TDD([makeQuery(id+"F15.boolean.opBoolean","COPY",EDGE,{"derivedFrom":makeQuery(id+"F15.opExtrude","CAP_EDGE",EDGE,{"disambiguationData":[OSD([subQ0])],"isStart":false})})])]})]});}
            var Q17;
            {var subQ0=sQuery(id+"F9.wireOp",EDGE,"E43.left");var subQ1=sQuery(id+"F9.wireOp",EDGE,"E43.top");var subQ4=makeQuery(id+"F10.opExtrude","SWEPT_FACE",FACE,{"disambiguationData":[OSD([subQ0])]});var subQ6=makeQuery(id+"F15.opExtrude","CAP_FACE",FACE,{"disambiguationData":[OSD([subQ1])],"isStart":false});Q17=makeQuery(id+"F17.boolean.opBoolean","MERGE",EDGE,{"derivedFrom":[makeQuery(id+"F15.boolean.opBoolean","COPY",EDGE,{"disambiguationData":[topologyDisambiguationEdgeConnected([subQ4,subQ6]),TD([makeQuery(id+"F15.opExtrude","SWEPT_FACE",FACE,{"disambiguationData":[OSD([subQ1])]})])],"derivedFrom":makeQuery(id+"F15.opExtrude","CAP_EDGE",EDGE,{"disambiguationData":[OSD([subQ1,subQ0])],"isStart":false})}),makeQuery(id+"F17.opExtrude","SWEPT_EDGE",EDGE,{"disambiguationData":[OSD([subQ1,subQ0]),TDD([makeQuery(id+"F15.boolean.opBoolean","COPY",VERTEX,{"derivedFrom":makeQuery(id+"F15.opExtrude","CAP_VERTEX",VERTEX,{"disambiguationData":[OSD([subQ1,subQ0])],"isStart":false})})])]})]});}
            fillet(context, id + "F19", {"entities" : qUnion([Q0, Q1, Q2, Q3, Q4, Q5, Q6, Q7, Q8, Q9, Q10, Q11, Q12, Q13, Q14, Q15, Q16, Q17]), "radius" : 0.25 * mm, "tangentPropagation" : true, "allowEdgeOverflow" : false});
        }
        {
            var Q0;
            Q0=qCreatedBy(makeId("Front.planeOp"),FACE);
            var sketch = newSketch(context, id + "F20", { "sketchPlane" : qUnion([Q0])});
            skLineSegment(sketch, "E52", {"start": v(0, 0) * mm, "end": v(2.5, 0) * mm});
            skLineSegment(sketch, "E53", {"start": v(2.5, 0) * mm, "end": v(2.5, 63.5) * mm});
            skLineSegment(sketch, "E54", {"start": v(2.5, 63.5) * mm, "end": v(0.5, 63.5) * mm});
            skLineSegment(sketch, "E55", {"start": v(2.5, 63.5) * mm, "end": v(4.5, 63.5) * mm});
            skArc(sketch, "E56", {"start": v(4.5, 63.5) * mm, "mid": v(2.5, 68.74) * mm, "end": v(0.5, 63.5) * mm});
            skArc(sketch, "E57.0", {"start": v(5.17, 62.75) * mm, "mid": v(2.5, 69.74) * mm, "end": v(-0.17, 62.75) * mm});
            skLineSegment(sketch, "E58", {"start": v(-0.17, 62.75) * mm, "end": v(0.5, 63.5) * mm});
            skLineSegment(sketch, "E59", {"start": v(4.5, 63.5) * mm, "end": v(5.17, 62.75) * mm});
            skSolve(sketch);
        }
        {
            var Q0;
            Q0=makeQuery(id+"F20.imprint","IMPRINT",FACE,{"disambiguationData":[TD([[makeQuery(id+"F20.imprint","IMPRINT",EDGE,{"derivedFrom":sQuery(id+"F20.wireOp",EDGE,"E56")}),-1.0]])]});
            extrude(context, id + "F21", {"entities" : qUnion([Q0]), "operationType" : NewBodyOperationType.ADD, "endBound" : BoundingType.SYMMETRIC, "depth" : 2 * mm, "offsetDistance" : 25 * mm});
        }
    });
